# Revit family: Trim-Handle-Waterworks-Flyte-Pressure_Balance
name_source: partatom
category: Plumbing Fixtures
revit_build: Autodesk Revit MEP 2014 (Build: 20140709_2115(x64)
units: mm (PartAtom-declared; Revit-internal decimal feet)

## types (8) — shared parameters
ADA Compliant = Yes
Anti-scald Protection = No
Assembly Code = D2010
CW Connection = Yes
Certification IAPMO = Yes
Certification State of MA = Yes
Certification cUPC = Yes
Control Valve Rough-in Depth Maximum = 0' - 2 7/8"
Control Valve Rough-in Depth Minimum = 0' - 2 3/8"
Default Elevation = 2' - 10"
Depth = 0' - 3 1/16"
Diverter Valve Rough-in Depth Maximum = 0' - 3 5/8"
Diverter Valve Rough-in Depth Minimum = 0' - 3 1/8"
Fittings Hole Diameter = 0' - 3 1/2"
HW Connection = Yes
Height = 0' - 5 7/8"
Hot Limit Safety Stop = No
Keynote = 22 40 00
Length = 0' - 5 1/2"
Manufacturer = Waterworks
Product Documentation Link = http://assets.waterworks.com
Product Page URL = http://www.waterworks.com
URL = http://www.waterworks.com
Vent Connection = No
Version = 2014 - v1.0a
Warranty = http://www.waterworks.com
Waste Connection = No
zero-valued in all types: CWFU, HWFU, WFU

## per-type parameters (varying)
| type | Code Compliance | Constraint | ControlM | Description | Finish | Model | Model SKU | Product Name | With Diverter | Without Diverter | ‌Installation Requirements or Notes |
| Control Valve Trim, in Chrome | Code # FLPB10: Complies with ASME A112.18.1/CSA B125.1, ANSI A117.1 ADA. Certified with IAPMO, cUPC & State of MA | 1 | 1 | Flyte Pressure Balance Control Valve Trim with Metal Lever Handle in Chrome | Metal - Waterworks - Chrome | FLPB10 | 05-88303-38547 | Flyte Pressure Balance Control Valve Trim with Metal Lever Handle in Chrome | No | Yes | Requires valve rough GUPB81, item 26-19129-09166 sold separately |
| Control Valve Trim, in Graphite | Code # FLPB10: Complies with ASME A112.18.1/CSA B125.1, ANSI A117.1 ADA. Certified with IAPMO, cUPC & State of MA | 1 | 2 | Flyte Pressure Balance Control Valve Trim with Metal Lever Handle in Graphite | Metal - Waterworks - Graphite | FLPB10 | 05-58041-68076 | Flyte Pressure Balance Control Valve Trim with Metal Lever Handle in Graphite | No | Yes | Requires valve rough GUPB81, item 26-19129-09166 sold separately |
| Control Valve Trim, in Nickel | Code # FLPB10: Complies with ASME A112.18.1/CSA B125.1, ANSI A117.1 ADA. Certified with IAPMO, cUPC & State of MA | 1 | 3 | Flyte Pressure Balance Control Valve Trim with Metal Lever Handle in Nickel | Metal - Waterworks - Nickel | FLPB10 | 05-46030-50091 | Flyte Pressure Balance Control Valve Trim with Metal Lever Handle in Nickel | No | Yes | Requires valve rough GUPB81, item 26-19129-09166 sold separately |
| Control Valve Trim, in Unlacquered Brass | Code # FLPB10: Complies with ASME A112.18.1/CSA B125.1, ANSI A117.1 ADA. Certified with IAPMO, cUPC & State of MA | 1 | 4 | Flyte Pressure Balance Control Valve Trim with Metal Lever Handle in Unlacquered Brass | Metal - Waterworks - Unlacquered Brass | FLPB10 | 05-36695-83990 | Flyte Pressure Balance Control Valve Trim with Metal Lever Handle in Unlacquered Brass | No | Yes | Requires valve rough GUPB81, item 26-19129-09166 sold separately |
| Diverter Trim, in Chrome | Code # FLPB30: Complies with ASME A112.18.1/CSA B125.1, ANSI A117.1 ADA. Certified with IAPMO, cUPC & State of MA | 2 | 5 | Flyte Pressure Balance with Diverter Trim with Metal Lever Handle in Chrome | Metal - Waterworks - Chrome | FLPB30 | 05-91621-16917 | Flyte Pressure Balance with Diverter Trim with Metal Lever Handle in Chrome | Yes | No | Requires valve rough GUPB87, item 26-50948-33633 sold separately |
| Diverter Trim, in Graphite | Code # FLPB30: Complies with ASME A112.18.1/CSA B125.1, ANSI A117.1 ADA. Certified with IAPMO, cUPC & State of MA | 2 | 6 | Flyte Pressure Balance with Diverter Trim with Metal Lever Handle in Graphite | Metal - Waterworks - Graphite | FLPB30 | 05-58660-46819 | Flyte Pressure Balance with Diverter Trim with Metal Lever Handle in Graphite | Yes | No | Requires valve rough GUPB87, item 26-50948-33633 sold separately |
| Diverter Trim, in Nickel | Code # FLPB30: Complies with ASME A112.18.1/CSA B125.1, ANSI A117.1 ADA. Certified with IAPMO, cUPC & State of MA | 2 | 7 | Flyte Pressure Balance with Diverter Trim with Metal Lever Handle in Nickel | Metal - Waterworks - Nickel | FLPB30 | 05-07676-17315 | Flyte Pressure Balance with Diverter Trim with Metal Lever Handle in Nickel | Yes | No | Requires valve rough GUPB87, item 26-50948-33633 sold separately |
| Diverter Trim, in Unlacquered Brass | Code # FLPB30: Complies with ASME A112.18.1/CSA B125.1, ANSI A117.1 ADA. Certified with IAPMO, cUPC & State of MA | 2 | 8 | Flyte Pressure Balance with Diverter Trim with Metal Lever Handle in Unlacquered Brass | Metal - Waterworks - Unlacquered Brass | FLPB30 | 05-46703-52856 | Flyte Pressure Balance with Diverter Trim with Metal Lever Handle in Unlacquered Brass | Yes | No | Requires valve rough GUPB87, item 26-50948-33633 sold separately |

## geometry (parser evidence)
native form markers: Sweep x6
no freeform markers — native parametric forms only
